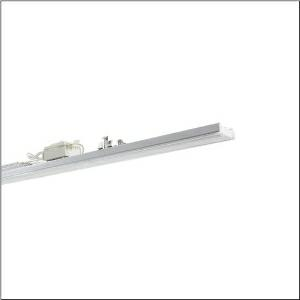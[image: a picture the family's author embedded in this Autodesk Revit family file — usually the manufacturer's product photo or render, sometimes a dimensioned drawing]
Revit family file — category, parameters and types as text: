
# Revit family: licross_11_recessed_mo_51tl12dv4fxgd
name_source: partatom
category: Lighting Fixtures
units: mm (PartAtom-declared; Revit-internal decimal feet)

## family parameters
Cut with Voids When Loaded = No
Host = Face
Light Source = No
Part Type = Normal
Room Calculation Point = No
Round Connector Dimension = Use Diameter
Shared = No

## types (1)
- --- (1 x LED, 2300 lm, 12.5 W, 4000K)
    Apparent Load = 13 VA
    CIE Flux Codes = 67 92 99 100 100
    Color Rendering = 80
    Color Temperature = 4000K
    Default Elevation = 1800 mm
    Description = Licross 11 Recessed MO, luminaire insert, of sheet steel, coil coated, white, length: 2.250mm, width: 66mm, height: 67mm, LED rated luminous flux: 15.360lm, light colour: 840, SDCM (Standard Deviation of Colour Matching)MacAdam ≤ 2 SDCM (initial), control gear: DALI 2 (for two DALI lines), with plug, 6-pole, with phase selection, mains connection: 220..240V, AC/DC, 0/50..60Hz, rated input power: 84W, without changeover relay, for emergency light function, for central battery installations according to EN 60598-2-22, internal wiring halogen-free, primary optical cover: cover, of PMMA, light emission: direct distribution, primary light characteristic: symmetric, protection rating (complete): IP40, insulation class (complete): insulation class I (protective earthing), certification: CE, ENEC, VDE, UKCA, protection symbol: D if used in an environment without relevant dust loads with corresponding accessories, impact resistance: IK06, permissible ambient temperature for indoor applications: -25..+35°C, standard: EN 60598-2-22, corresponds to IFS (International Featured Standards) requirements for safety and quality in the food industry, reducing of maximum allowable ambient temperature of 5°C with ceiling mounting, LABS conformity tested according to VDMA 24364:2018-05, The light source and the operating device comply with the requirements of the Ecodesign Regulation (EU) 2019/2020 and are replaceable in accordance with this regulation, packaging unit: 1 piece
    Height = 58 mm
    Lamp = 1 x LED
    Lamp Light Flux = 2300 lm
    Lamp Power = 12.5 W
    Lamp count = 1
    Length = 2250 mm
    Luminous efficacy = 184 lm/W
    Manufacturer = Siteco
    ModVariant = No
    Model = 51TL12DV4FXGD
    Mounting Place = Ceiling
    Mounting Type = Pendant
    Number of Poles = 1
    OnlyDefault = Yes
    Power Factor = 1
    Product Name = Licross 11 Recessed MO
    Product group = luminaire insert | ceiling pendant
    ProductGroupID = 901
    Protection Class = Protection class I
    Protection Degree = IP 40
    RLX_Detail_Level = 1
    RLX_Emergency_Light_Flux = 0 lm
    RLX_Emergency_Type = 0
    RLX_Emergency_Type_DB = No
    RlxData = <blob elided: 30001 chars, md5=548b2d19>
    Socket = socket
    Standby Power = 0 W
    System Light Flux = 2300 lm
    System Power = 13 W
    Type Comments = : DC mode (central or group accumulator) initial emergency light level
    Type Image = l_1296930.jpg
    URL = http://relux.com
    VarID = @adj_091529
    Voltage = 0 V
    Weight = 0.00 kg
    Width = 66 mm

## geometry (parser evidence)
native form markers: Blend x4, Sweep x10
no freeform markers — native parametric forms only
